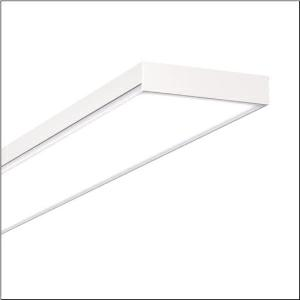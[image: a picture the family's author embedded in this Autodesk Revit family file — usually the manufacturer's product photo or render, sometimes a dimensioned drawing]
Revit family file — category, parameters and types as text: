
# Revit family: apollon_31_surface_51mp26wm2441wa
name_source: partatom
category: Lighting Fixtures
units: mm (PartAtom-declared; Revit-internal decimal feet)

## family parameters
Cut with Voids When Loaded = No
Host = Face
Light Source = No
Part Type = Normal
Room Calculation Point = No
Round Connector Dimension = Use Diameter
Shared = No

## types (1)
- Apollon 31 Surface (1 x LED, 4600 lm, 33 W, 4000K)
    Apparent Load = 33 VA
    CIE Flux Codes = 61 87 97 97 100
    Color Rendering = 80
    Color Temperature = 4000K
    Default Elevation = 1800 mm
    Description = Apollon 31 Surface, office luminaire, primary optical cover: micro prismatic cover, of PMMA, light emission: direct distribution, primary light characteristic: symmetric, installation type: surface-mounted, LED, rated luminous flux: 4.600lm, luminous efficacy: 139lm/W, light colour: 840, colour temperature: 4000K, control gear: ON/OFF Multilumen, with terminal, 3-pole, mains connection: 220..240V, AC, 50/60Hz, rated input power: 33W, housing, of sheet steel, coated, traffic white (RAL 9016), length: 1.545mm, width: 200mm, height: 44mm, protection rating (complete): IP20, protection rating (on room side): IP40, protection rating (lamp compartment, on room side): IP40, insulation class (complete): insulation class I (protective earthing), certification: CE, ENEC, UKCA, impact resistance: IK02, permissible operating ambient temperature: -20..+40°C, packaging unit: 1 piece
    Height = 44 mm
    Lamp = 1 x LED
    Lamp Light Flux = 4600 lm
    Lamp Power = 33 W
    Lamp count = 1
    Length = 1545 mm
    Luminous efficacy = 139 lm/W
    Manufacturer = Siteco
    ModVariant = No
    Model = 51MP26WM2441WA
    Mounting Place = Ceiling
    Mounting Type = Surface mounted
    Number of Poles = 1
    OnlyDefault = Yes
    Power Factor = 1
    Product Name = Apollon 31 Surface
    Product group = office luminaire | ceiling mounted
    ProductGroupID = 301
    Protection Class = Protection class I
    Protection Degree = IP 20
    RLX_Detail_Level = 1
    RLX_Emergency_Light_Flux = 0 lm
    RLX_Emergency_Type = 0
    RLX_Emergency_Type_DB = No
    RlxData = <blob elided: 20797 chars, md5=655af65a>
    Socket = socket
    Standby Power = 0 W
    System Light Flux = 4600 lm
    System Power = 33 W
    Type Comments = Product without accessories
    Type Image = l_1313658.jpg
    URL = http://relux.com
    VarID = ---
    Voltage = 0 V
    Weight = 0.00 kg
    Width = 200 mm

## geometry (parser evidence)
native form markers: Blend x4, Sweep x10
no freeform markers — native parametric forms only
